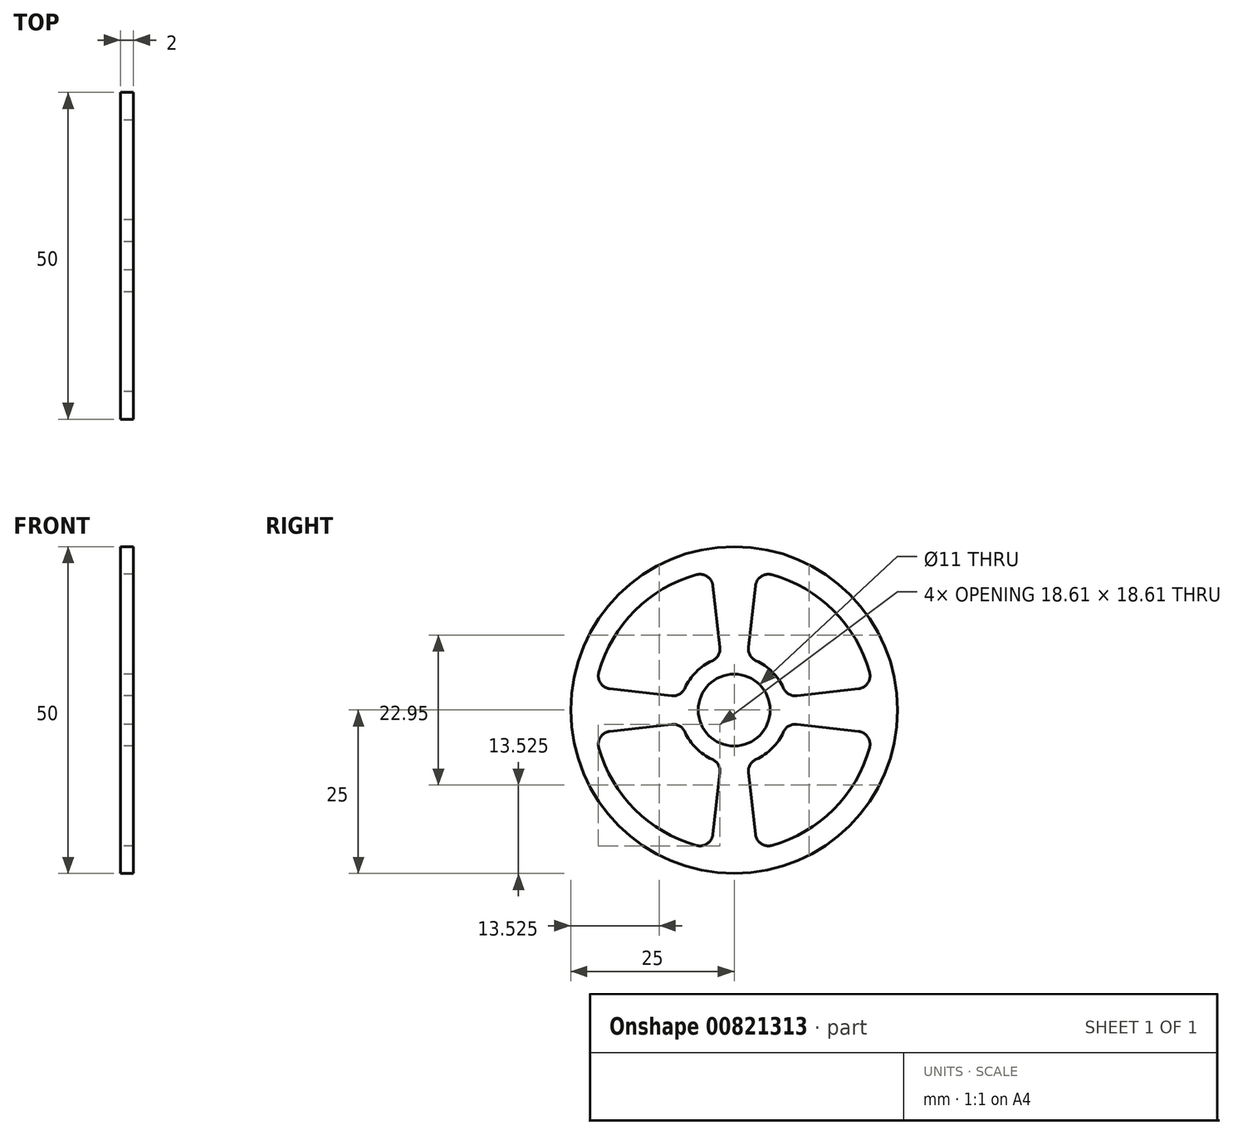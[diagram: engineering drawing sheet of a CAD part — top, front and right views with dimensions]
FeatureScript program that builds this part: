
annotation { "Feature Type Name" : "Feature", "Feature Type Description" : "" }
export const myFeature = defineFeature(function(context is Context, id is Id, definition is map)
    precondition{}
    {
        {
            var Q0;
            Q0=qCreatedBy(makeId("Right.planeOp"),FACE);
            var sketch = newSketch(context, id + "F0", { "sketchPlane" : qUnion([Q0])});
            skCircle(sketch, "E0", {"center": v(0, 0) * mm, "radius": 25 * mm});
            skArc(sketch, "E1", {"start": v(-5.77, 20.71) * mm, "mid": v(-15.2, 15.2) * mm, "end": v(-20.71, 5.77) * mm});
            skArc(sketch, "E2", {"start": v(-3.35, 7.54) * mm, "mid": v(-5.83, 5.83) * mm, "end": v(-7.54, 3.35) * mm});
            skCircle(sketch, "E3", {"center": v(0, 0) * mm, "radius": 5.5 * mm});
            skLineSegment(sketch, "E4", {"start": v(-3.25, 19) * mm, "end": v(-2.18, 9.6) * mm});
            skLineSegment(sketch, "E5", {"start": v(3.25, 19) * mm, "end": v(2.18, 9.6) * mm});
            skPoint(sketch, "E6.start.orphan", {"position": v(0, 8.25) * mm});
            skLineSegment(sketch, "E7.1.0", {"start": v(-19, -3.25) * mm, "end": v(-9.6, -2.18) * mm});
            skLineSegment(sketch, "E7.1.1", {"start": v(-19, 3.25) * mm, "end": v(-9.6, 2.18) * mm});
            skLineSegment(sketch, "E7.2.0", {"start": v(3.25, -19) * mm, "end": v(2.18, -9.6) * mm});
            skLineSegment(sketch, "E7.2.1", {"start": v(-3.25, -19) * mm, "end": v(-2.18, -9.6) * mm});
            skLineSegment(sketch, "E7.3.0", {"start": v(19, 3.25) * mm, "end": v(9.6, 2.18) * mm});
            skLineSegment(sketch, "E7.3.1", {"start": v(19, -3.25) * mm, "end": v(9.6, -2.18) * mm});
            skArc(sketch, "E8.trimOffspring", {"start": v(-20.71, -5.77) * mm, "mid": v(-15.2, -15.2) * mm, "end": v(-5.77, -20.71) * mm});
            skArc(sketch, "E9.trimOffspring", {"start": v(-7.54, -3.35) * mm, "mid": v(-5.83, -5.83) * mm, "end": v(-3.35, -7.54) * mm});
            skArc(sketch, "E10.trimOffspring", {"start": v(7.54, 3.35) * mm, "mid": v(5.83, 5.83) * mm, "end": v(3.35, 7.54) * mm});
            skArc(sketch, "E11.trimOffspring", {"start": v(3.35, -7.54) * mm, "mid": v(5.83, -5.83) * mm, "end": v(7.54, -3.35) * mm});
            skArc(sketch, "E12.trimOffspring", {"start": v(20.71, 5.77) * mm, "mid": v(15.2, 15.2) * mm, "end": v(5.77, 20.71) * mm});
            skArc(sketch, "E13.trimOffspring", {"start": v(5.77, -20.71) * mm, "mid": v(15.2, -15.2) * mm, "end": v(20.71, -5.77) * mm});
            skPoint(sketch, "E14.visualSharp", {"position": v(-8, 2) * mm});
            skArc(sketch, "E14.filletArc", {"start": v(-9.6, 2.18) * mm, "mid": v(-8.37, 2.43) * mm, "end": v(-7.54, 3.35) * mm});
            skPoint(sketch, "E15.visualSharp", {"position": v(-2, 8) * mm});
            skArc(sketch, "E15.filletArc", {"start": v(-3.35, 7.54) * mm, "mid": v(-2.43, 8.37) * mm, "end": v(-2.18, 9.6) * mm});
            skPoint(sketch, "E16.visualSharp", {"position": v(-3.5, 21.21) * mm});
            skArc(sketch, "E16.filletArc", {"start": v(-3.25, 19) * mm, "mid": v(-4.12, 20.44) * mm, "end": v(-5.77, 20.71) * mm});
            skPoint(sketch, "E17.visualSharp", {"position": v(-21.21, 3.5) * mm});
            skArc(sketch, "E17.filletArc", {"start": v(-20.71, 5.77) * mm, "mid": v(-20.44, 4.12) * mm, "end": v(-19, 3.25) * mm});
            skPoint(sketch, "E18.visualSharp", {"position": v(-21.21, -3.5) * mm});
            skArc(sketch, "E18.filletArc", {"start": v(-19, -3.25) * mm, "mid": v(-20.44, -4.12) * mm, "end": v(-20.71, -5.77) * mm});
            skPoint(sketch, "E19.visualSharp", {"position": v(-8, -2) * mm});
            skArc(sketch, "E19.filletArc", {"start": v(-7.54, -3.35) * mm, "mid": v(-8.37, -2.43) * mm, "end": v(-9.6, -2.18) * mm});
            skPoint(sketch, "E20.visualSharp", {"position": v(-2, -8) * mm});
            skArc(sketch, "E20.filletArc", {"start": v(-2.18, -9.6) * mm, "mid": v(-2.43, -8.37) * mm, "end": v(-3.35, -7.54) * mm});
            skPoint(sketch, "E21.visualSharp", {"position": v(-3.5, -21.21) * mm});
            skArc(sketch, "E21.filletArc", {"start": v(-5.77, -20.71) * mm, "mid": v(-4.12, -20.44) * mm, "end": v(-3.25, -19) * mm});
            skPoint(sketch, "E22.visualSharp", {"position": v(3.5, -21.21) * mm});
            skArc(sketch, "E22.filletArc", {"start": v(3.25, -19) * mm, "mid": v(4.12, -20.44) * mm, "end": v(5.77, -20.71) * mm});
            skPoint(sketch, "E23.visualSharp", {"position": v(2, -8) * mm});
            skArc(sketch, "E23.filletArc", {"start": v(3.35, -7.54) * mm, "mid": v(2.43, -8.37) * mm, "end": v(2.18, -9.6) * mm});
            skPoint(sketch, "E24.visualSharp", {"position": v(21.21, -3.5) * mm});
            skArc(sketch, "E24.filletArc", {"start": v(20.71, -5.77) * mm, "mid": v(20.44, -4.12) * mm, "end": v(19, -3.25) * mm});
            skPoint(sketch, "E25.visualSharp", {"position": v(8, -2) * mm});
            skArc(sketch, "E25.filletArc", {"start": v(9.6, -2.18) * mm, "mid": v(8.37, -2.43) * mm, "end": v(7.54, -3.35) * mm});
            skPoint(sketch, "E26.visualSharp", {"position": v(8, 2) * mm});
            skArc(sketch, "E26.filletArc", {"start": v(7.54, 3.35) * mm, "mid": v(8.37, 2.43) * mm, "end": v(9.6, 2.18) * mm});
            skPoint(sketch, "E27.visualSharp", {"position": v(21.21, 3.5) * mm});
            skArc(sketch, "E27.filletArc", {"start": v(19, 3.25) * mm, "mid": v(20.44, 4.12) * mm, "end": v(20.71, 5.77) * mm});
            skPoint(sketch, "E28.visualSharp", {"position": v(3.5, 21.21) * mm});
            skArc(sketch, "E28.filletArc", {"start": v(5.77, 20.71) * mm, "mid": v(4.12, 20.44) * mm, "end": v(3.25, 19) * mm});
            skPoint(sketch, "E29.visualSharp", {"position": v(2, 8) * mm});
            skArc(sketch, "E29.filletArc", {"start": v(2.18, 9.6) * mm, "mid": v(2.43, 8.37) * mm, "end": v(3.35, 7.54) * mm});
            skSolve(sketch);
        }
        {
            var Q0;
            Q0 = qSketchRegion(id + "F0", true);
            extrude(context, id + "F1", {"entities" : qUnion([Q0]), "depth" : 2 * mm, "offsetDistance" : 25 * mm});
        }
    });
